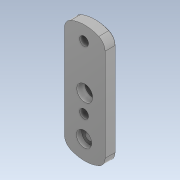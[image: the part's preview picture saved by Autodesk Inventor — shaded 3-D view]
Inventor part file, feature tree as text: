
AUTODESK INVENTOR PART (.ipt)
format: ipt  version: 2022.1 (Build 261234020, 234B)  size: 193,536 bytes
history: native  units: mm
features: chamfer x5, sketch x4, other x3, extrude x2, hole x2, reference x2, direct_edit x1, delete_face x1, projected_geometry x1, move_body x1
ambient origin geometry x8: Origin, YZ Plane, XZ Plane, XY Plane, X Axis, Y Axis, Z Axis, Center Point
bodies: Volumenkörper1 (feature_tree)
feature tree (22):
  extrude  "Extrusion1"  Depth=44.911893mm
  hole  "Bohrung1"  [1 undecoded]
  hole  "Bohrung2"  [1 undecoded]
  direct_edit  "Direktbearbeitung1"
  extrude  "Extrusion4"  Depth=2.0mm
  chamfer  "Fase1"  Distance=2.4mm
  chamfer  "Fase2"  Distance=3.0mm
  delete_face  "Fläche löschen1"
  chamfer  "Fase3"  Distance=2.0mm Angle=45.0deg
  chamfer  "Fase4"  Distance=2.4mm
  chamfer  "Fase5"  Distance=2.4mm
  sketch  "Skizze1"  dims[d0=5.0mm d1=0.0mm d2=44.911893mm]
  reference  "Referenz1"
  sketch  "Skizze2"  dims[d3=15.5mm d4=22.455947mm]
  projected_geometry  "Projizierte Kontur1"
  sketch  "Skizze4"  dims[d5=0.0mm]
  reference  "Referenz6"
  sketch  "Skizze6"  dims[d6=6.05mm d7=6.0mm d8=4.0mm d9=2.0mm d10=90.0deg d11=3.1mm d12=0.0mm d19=3.3mm d20=6.0mm d21=5.8mm d22=2.0mm d23=14.3117mm d24=5.0mm d25=0.0mm d26=0.0mm d27=0.0mm d28=-1.0mm d37=2.4mm d38=2.4mm d39=3.0mm d40=0.0mm d41=0.6mm d42=2.0mm d43=45.0deg d44=2.4mm d45=2.4mm d46=2.4mm d47=2.4mm d48=0.4mm d49=2.0mm d50=9.599311mm d51=0.2mm d52=2.0mm d53=45.0deg d54=0.4mm d55=2.0mm d56=45.0deg d57=0.2mm d58=2.0mm d59=45.0deg]
  other  "<userpath>\Desktop\Voron-2-2.4r1\Custom\Front_Idlers\Baugruppe1.iam"
  other  "Baugruppe1.iam"
  other  "Front_Idler1:1"
  move_body  "Verschieben1"
note: 2 required parameter values undecoded (feature->parameter linkage not recoverable at this tier; creation-order binding heuristic only, values carry confidence <= 0.55)
